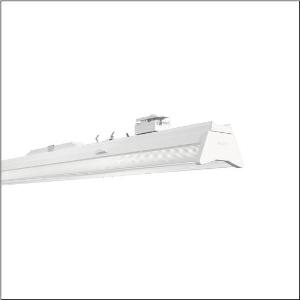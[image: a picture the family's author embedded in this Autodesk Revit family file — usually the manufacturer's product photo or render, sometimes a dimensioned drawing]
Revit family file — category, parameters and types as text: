
# Revit family: licross_r__21_performance_mo_52td16vn455g_74b2
name_source: partatom
category: Lighting Fixtures
units: mm (PartAtom-declared; Revit-internal decimal feet)

## family parameters
Cut with Voids When Loaded = No
Host = Face
Light Source = No
Part Type = Normal
Room Calculation Point = No
Round Connector Dimension = Use Diameter
Shared = No

## types (1)
- --- (1 x LED, 5500 lm, 30 W, 4000K)
    Apparent Load = 30 VA
    CIE Flux Codes = 66 88 96 79 100
    Color Rendering = 80
    Color Temperature = 4000K
    Default Elevation = 1800 mm
    Description = Licross® 21 Performance MO, luminaire insert, of sheet steel, galvanised, coil coated, white, length: 1.500mm, width: 120mm, height: 123mm, LED rated luminous flux: 5.500lm, light colour: 840, SDCM (Standard Deviation of Colour Matching)MacAdam ≤ 3 SDCM (initial), control gear: DALI 2, CLO, with plug, 5-pole, with phase selection, mains connection: 220..240V, AC, 50/60Hz, start of lifetime: 30W, end of service life: 36W, internal wiring halogen-free, primary light control with lens, of plastic, primary optical cover: cover, of PMMA, light emission: direct/indirect distribution, primary light characteristic: symmetric, protection rating (complete): IP54, insulation class (complete): insulation class I (protective earthing), certification: CE, ENEC, VDE, UKCA, protection symbol: D if used in an environment with non-conductive dust loads with corresponding accessories, impact resistance: IK06, permissible ambient temperature for indoor applications: -25..+50°C, corresponds to IFS (International Featured Standards) requirements for safety and quality in the food industry, reducing of maximum allowable ambient temperature of 5°C with ceiling mounting, LABS conformity tested according to VDMA 24364:2018-05, packaging unit: 1 piece
    Height = 114 mm
    Lamp = 1 x LED
    Lamp Light Flux = 5500 lm
    Lamp Power = 30 W
    Lamp count = 1
    Length = 1500 mm
    Luminous efficacy = 183 lm/W
    Manufacturer = Siteco
    ModVariant = No
    Model = 52TD16VN455G
    Mounting Place = Ceiling
    Mounting Type = Pendant
    Number of Poles = 1
    OnlyDefault = Yes
    Power Factor = 1
    Product Name = Licross® 21 Performance MO
    Product group = luminaire insert | ceiling pendant
    ProductGroupID = 901
    Protection Class = Protection class I
    Protection Degree = IP 54
    RLX_Detail_Level = 1
    RLX_Emergency_Light_Flux = 0 lm
    RLX_Emergency_Type = 0
    RLX_Emergency_Type_DB = No
    RlxData = <blob elided: 33641 chars, md5=a35b3b07>
    Socket = socket
    Standby Power = 0 W
    System Light Flux = 5500 lm
    System Power = 30 W
    Type Comments = factory setting: luminous flux: 100 % | dim-lin: 254 | 203 mA
    Type Image = l_1256138.jpg
    URL = http://relux.com
    VarID = @adj_090671
    Voltage = 0 V
    Weight = 0.00 kg
    Width = 120 mm

## geometry (parser evidence)
native form markers: Blend x4, Sweep x10
no freeform markers — native parametric forms only
